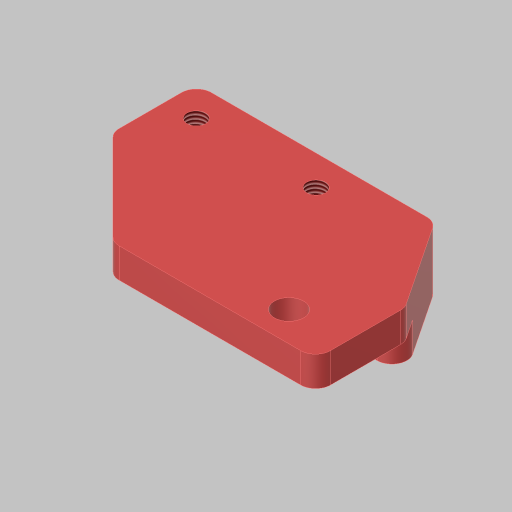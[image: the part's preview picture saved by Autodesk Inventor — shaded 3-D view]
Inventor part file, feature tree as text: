
AUTODESK INVENTOR PART (.ipt)
format: ipt  version: 2023.5 (Build 275446000, 446)  size: 187,392 bytes
history: native  units: in
note: dims shown in document units (in); Inventor stores cm internally (conversion verified against a paired STEP export)
features: sketch x6, extrude x3, fillet x3, hole x2, projected_geometry x2
ambient origin geometry x8: Origin, YZ Plane, XZ Plane, XY Plane, X Axis, Y Axis, Z Axis, Center Point
bodies: Solid1 (feature_tree)
feature tree (16):
  extrude  "Extrusion1"  Depth=1.5in
  hole  "Hole1"  [1 undecoded]
  hole  "Hole2"  [1 undecoded]
  fillet  "Fillet1"  Radius=0.125in
  extrude  "Extrusion2"  Depth=0.125in
  fillet  "Fillet2"  Radius=0.5in
  sketch  "Sketch5"  dims[d14=0.244in d15=0.75in d16=0.375in d17=0.25in d18=0.5635in d19=1.0in d20=0.8108in d21=0.125in]
  extrude  "Extrusion3"  Depth=0.25in TaperAngle=0.0deg
  fillet  "Fillet3"  Radius=0.125in
  sketch  "Sketch1"  dims[d0=2.5in d1=1.5in]
  sketch  "Sketch2"  dims[d2=0.25in d3=0.0in d4=1.005in]
  sketch  "Sketch3"  dims[d5=0.25in]
  sketch  "Sketch4"  dims[d6=0.156in d7=0.38in d8=0.385in d9=0.25in d10=0.5635in d11=1.0in d12=0.8108in d13=0.25in]
  sketch  "Sketch6"  dims[d22=0.25in d23=0.75in d24=0.5in d25=0.25in d26=0.0in d27=0.125in d28=0.777in d29=0.8in d30=0.8in d31=0.25in d32=0.0in d33=0.125in]
  projected_geometry  "Projected Loop1"
  projected_geometry  "Project Cut Edges1"
note: 2 required parameter values undecoded (feature->parameter linkage not recoverable at this tier; creation-order binding heuristic only, values carry confidence <= 0.55)
